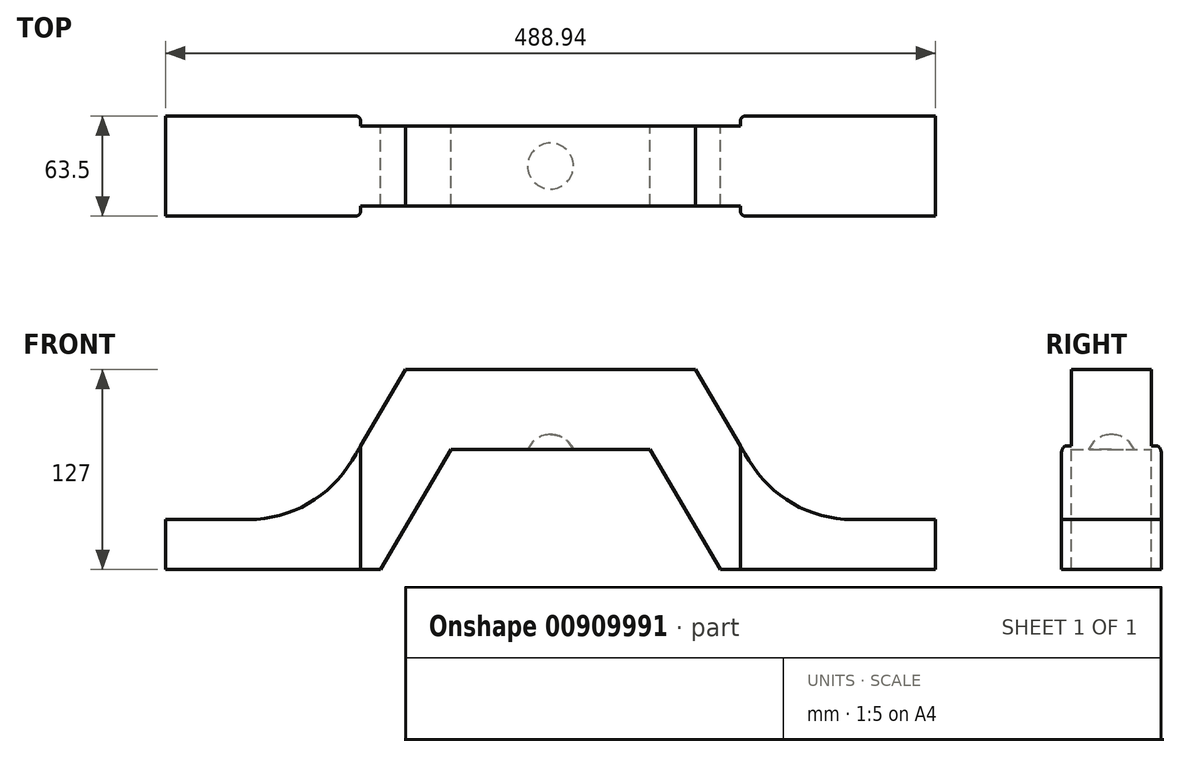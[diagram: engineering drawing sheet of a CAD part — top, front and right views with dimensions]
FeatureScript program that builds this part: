
annotation { "Feature Type Name" : "Feature", "Feature Type Description" : "" }
export const myFeature = defineFeature(function(context is Context, id is Id, definition is map)
    precondition{}
    {
        {
            var Q0;
            Q0=qCreatedBy(makeId("Front.planeOp"),FACE);
            var sketch = newSketch(context, id + "F0", { "sketchPlane" : qUnion([Q0])});
            skLineSegment(sketch, "E0", {"start": v(-63.05, 0) * mm, "end": v(63.05, 0) * mm});
            skLineSegment(sketch, "E1", {"start": v(63.05, 0) * mm, "end": v(107.95, -76.2) * mm});
            skLineSegment(sketch, "E2", {"start": v(107.95, -76.2) * mm, "end": v(120.65, -76.2) * mm});
            skLineSegment(sketch, "E3", {"start": v(244.48, -76.2) * mm, "end": v(244.48, -44.45) * mm});
            skLineSegment(sketch, "E4", {"start": v(244.48, -44.45) * mm, "end": v(191.75, -44.45) * mm});
            skLineSegment(sketch, "E5", {"start": v(126.1, -6.94) * mm, "end": v(92.08, 50.8) * mm});
            skLineSegment(sketch, "E6", {"start": v(92.08, 50.8) * mm, "end": v(-92.08, 50.8) * mm});
            skLineSegment(sketch, "E7", {"start": v(-92.07, 50.8) * mm, "end": v(-126.1, -6.94) * mm});
            skLineSegment(sketch, "E8", {"start": v(-191.75, -44.45) * mm, "end": v(-244.47, -44.45) * mm});
            skLineSegment(sketch, "E9", {"start": v(-244.47, -44.45) * mm, "end": v(-244.47, -76.2) * mm});
            skLineSegment(sketch, "E10", {"start": v(-244.47, -76.2) * mm, "end": v(-120.65, -76.2) * mm});
            skLineSegment(sketch, "E11", {"start": v(-107.95, -76.2) * mm, "end": v(-63.05, 0) * mm});
            skLineSegment(sketch, "E12", {"start": v(0, 0) * mm, "end": v(0, 50.8) * mm, "construction": true});
            skPoint(sketch, "E13.visualSharp", {"position": v(-148.2, -44.45) * mm});
            skArc(sketch, "E13.filletArc", {"start": v(-191.75, -44.45) * mm, "mid": v(-153.94, -34.41) * mm, "end": v(-126.1, -6.94) * mm});
            skPoint(sketch, "E14.visualSharp", {"position": v(148.2, -44.45) * mm});
            skArc(sketch, "E14.filletArc", {"start": v(126.1, -6.94) * mm, "mid": v(153.94, -34.41) * mm, "end": v(191.75, -44.45) * mm});
            skLineSegment(sketch, "E15", {"start": v(-120.65, -76.2) * mm, "end": v(-120.65, 2.3) * mm});
            skLineSegment(sketch, "E16", {"start": v(120.65, -76.2) * mm, "end": v(120.65, 2.3) * mm});
            skLineSegment(sketch, "E17", {"start": v(-120.65, -76.2) * mm, "end": v(-107.95, -76.2) * mm});
            skLineSegment(sketch, "E18", {"start": v(120.65, -76.2) * mm, "end": v(244.48, -76.2) * mm});
            skArc(sketch, "E19", {"start": v(14.55, 0) * mm, "mid": v(8.7, 6.93) * mm, "end": v(0, 9.53) * mm});
            skLineSegment(sketch, "E20", {"start": v(0, 9.53) * mm, "end": v(0, 0) * mm});
            skSolve(sketch);
        }
        {
            var Q0;
            Q0=makeQuery(id+"F0.imprint","IMPRINT",FACE,{"disambiguationData":[TD([[makeQuery(id+"F0.imprint","IMPRINT",EDGE,{"derivedFrom":sQuery(id+"F0.wireOp",EDGE,"E0")}),1.0]])]});
            var Q1;
            {var subQ0=sQuery(id+"F0.wireOp",EDGE,"E19");Q1=makeQuery(id+"F0.imprint","IMPRINT",FACE,{"disambiguationData":[TD([[makeQuery(id+"F0.imprint","IMPRINT",EDGE,{"derivedFrom":subQ0}),1.0]])]});}
            extrude(context, id + "F1", {"entities" : qUnion([Q0, Q1]), "depth" : 50.8 * mm, "offsetDistance" : 25 * mm, "symmetric" : true});
        }
        {
            var Q0;
            Q0=makeQuery(id+"F0.imprint","IMPRINT",FACE,{"disambiguationData":[TD([[makeQuery(id+"F0.imprint","IMPRINT",EDGE,{"derivedFrom":sQuery(id+"F0.wireOp",EDGE,"E8")}),1.0]])]});
            var Q1;
            Q1=makeQuery(id+"F0.imprint","IMPRINT",FACE,{"disambiguationData":[TD([[makeQuery(id+"F0.imprint","IMPRINT",EDGE,{"derivedFrom":sQuery(id+"F0.wireOp",EDGE,"E3")}),1.0]])]});
            extrude(context, id + "F2", {"entities" : qUnion([Q0, Q1]), "operationType" : NewBodyOperationType.ADD, "depth" : 63.5 * mm, "offsetDistance" : 25 * mm, "symmetric" : true});
        }
        {
            var Q0;
            Q0=makeQuery(id+"F1.opExtrude","CAP_EDGE",EDGE,{"disambiguationData":[OSD([sQuery(id+"F0.wireOp",EDGE,"E15")])],"isStart":false});
            var Q1;
            Q1=makeQuery(id+"F2.opExtrude","CAP_EDGE",EDGE,{"disambiguationData":[OSD([sQuery(id+"F0.wireOp",EDGE,"E15")])],"isStart":false});
            var Q2;
            Q2=makeQuery(id+"F1.opExtrude","CAP_EDGE",EDGE,{"disambiguationData":[OSD([sQuery(id+"F0.wireOp",EDGE,"E15")])],"isStart":true});
            var Q3;
            Q3=makeQuery(id+"F2.opExtrude","CAP_EDGE",EDGE,{"disambiguationData":[OSD([sQuery(id+"F0.wireOp",EDGE,"E15")])],"isStart":true});
            var Q4;
            Q4=makeQuery(id+"F1.opExtrude","CAP_EDGE",EDGE,{"disambiguationData":[OSD([sQuery(id+"F0.wireOp",EDGE,"E16")])],"isStart":true});
            var Q5;
            Q5=makeQuery(id+"F2.opExtrude","CAP_EDGE",EDGE,{"disambiguationData":[OSD([sQuery(id+"F0.wireOp",EDGE,"E16")])],"isStart":true});
            var Q6;
            Q6=makeQuery(id+"F1.opExtrude","CAP_EDGE",EDGE,{"disambiguationData":[OSD([sQuery(id+"F0.wireOp",EDGE,"E16")])],"isStart":false});
            var Q7;
            Q7=makeQuery(id+"F2.opExtrude","CAP_EDGE",EDGE,{"disambiguationData":[OSD([sQuery(id+"F0.wireOp",EDGE,"E16")])],"isStart":false});
            fillet(context, id + "F3", {"entities" : qUnion([Q0, Q1, Q2, Q3, Q4, Q5, Q6, Q7]), "radius" : 3 * mm, "tangentPropagation" : true, "allowEdgeOverflow" : false});
        }
        {
            var Q0;
            {var subQ0=sQuery(id+"F0.wireOp",EDGE,"E19");Q0=makeQuery(id+"F0.imprint","IMPRINT",FACE,{"disambiguationData":[TD([[makeQuery(id+"F0.imprint","IMPRINT",EDGE,{"derivedFrom":subQ0}),1.0]])]});}
            var Q1;
            Q1=sQuery(id+"F0.wireOp",EDGE,"E20");
            revolve(context, id + "F4", {"operationType" : NewBodyOperationType.REMOVE, "surfaceOperationType" : NewSurfaceOperationType.NEW, "entities" : qUnion([Q0]), "axis" : qUnion([Q1]), "revolveType" : RevolveType.FULL, "oppositeDirection" : true});
        }
    });
